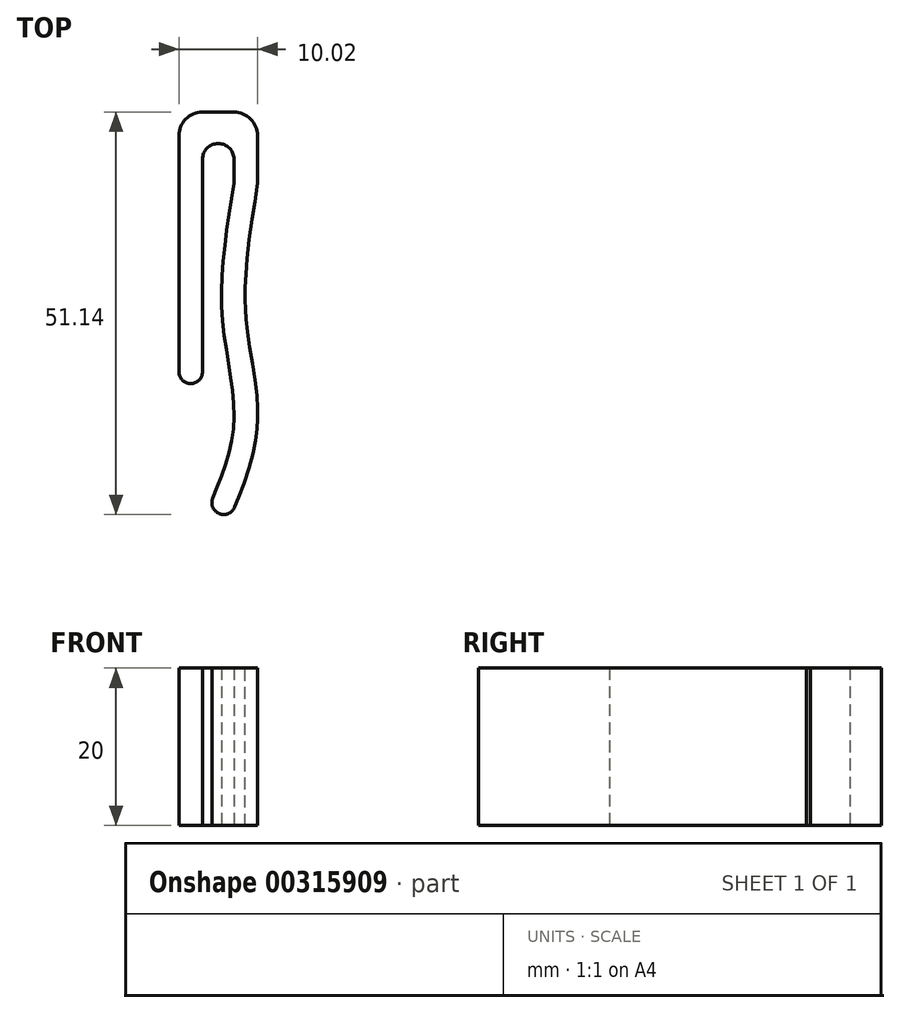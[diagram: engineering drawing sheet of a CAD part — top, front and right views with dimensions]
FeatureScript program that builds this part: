
annotation { "Feature Type Name" : "Feature", "Feature Type Description" : "" }
export const myFeature = defineFeature(function(context is Context, id is Id, definition is map)
    precondition{}
    {
        {
            var Q0;
            Q0=qCreatedBy(makeId("Top.planeOp"),FACE);
            var sketch = newSketch(context, id + "F0", { "sketchPlane" : qUnion([Q0])});
            skLineSegment(sketch, "E0.left", {"start": v(-12, 17.66) * mm, "end": v(-12, -12.34) * mm});
            skLineSegment(sketch, "E0.right", {"start": v(-9, 14.66) * mm, "end": v(-9, -12.34) * mm});
            skLineSegment(sketch, "E1.right", {"start": v(-2, 17.66) * mm, "end": v(-2, 14.66) * mm});
            skLineSegment(sketch, "E2.left", {"start": v(-2, 14.66) * mm, "end": v(-2, 11.66) * mm});
            skLineSegment(sketch, "E2.right", {"start": v(-5, 14.66) * mm, "end": v(-5, 11.66) * mm});
            skFitSpline(sketch, "E3", {"points": [v(-5, 11.66) * mm, v(-6.5, -5.15) * mm, v(-5, -18.43) * mm, v(-7.7, -28.42) * mm], "startDerivative": vector(-7.44, -45.92) * mm, "endDerivative": vector(-13.16, -32.95) * mm});
            skFitSpline(sketch, "E4.0", {"points": [v(-2.04, 11.18) * mm, v(-2.35, 9.27) * mm, v(-2.81, 6.43) * mm, v(-3.27, 2.76) * mm, v(-3.47, 0.53) * mm, v(-3.56, -1.21) * mm, v(-3.59, -2.5) * mm, v(-3.57, -3.54) * mm, v(-3.54, -4.37) * mm, v(-3.5, -5.19) * mm, v(-3.4, -6.2) * mm, v(-3.2, -7.86) * mm, v(-2.88, -9.94) * mm, v(-2.46, -12.48) * mm, v(-2.17, -14.63) * mm, v(-2.02, -16.37) * mm, v(-1.99, -17.48) * mm, v(-2, -18.37) * mm, v(-2.04, -19.27) * mm, v(-2.15, -20.36) * mm, v(-2.35, -21.64) * mm, v(-2.7, -23.28) * mm, v(-3.28, -25.23) * mm, v(-4.09, -27.44) * mm, v(-4.65, -28.85) * mm, v(-4.92, -29.53) * mm]});
            skArc(sketch, "E5", {"start": v(-7.7, -28.42) * mm, "mid": v(-6.87, -30.37) * mm, "end": v(-4.92, -29.53) * mm});
            skArc(sketch, "E6", {"start": v(-12, -12.34) * mm, "mid": v(-10.5, -13.84) * mm, "end": v(-9, -12.34) * mm});
            skLineSegment(sketch, "E7", {"start": v(-2.04, 11.18) * mm, "end": v(-2, 11.66) * mm});
            skArc(sketch, "E8", {"start": v(-9, 14.66) * mm, "mid": v(-7, 16.66) * mm, "end": v(-5, 14.66) * mm});
            skLineSegment(sketch, "E9", {"start": v(-9, 20.66) * mm, "end": v(-5, 20.66) * mm});
            skArc(sketch, "E10", {"start": v(-12, 17.66) * mm, "mid": v(-11.12, 19.78) * mm, "end": v(-9, 20.66) * mm});
            skArc(sketch, "E11", {"start": v(-5, 20.66) * mm, "mid": v(-2.88, 19.78) * mm, "end": v(-2, 17.66) * mm});
            skSolve(sketch);
        }
        {
            var Q0;
            Q0=qSketchRegion(id+"F0",true);
            extrude(context, id + "F1", {"entities" : qUnion([Q0]), "endBound" : BoundingType.SYMMETRIC, "depth" : 20 * mm});
        }
    });
